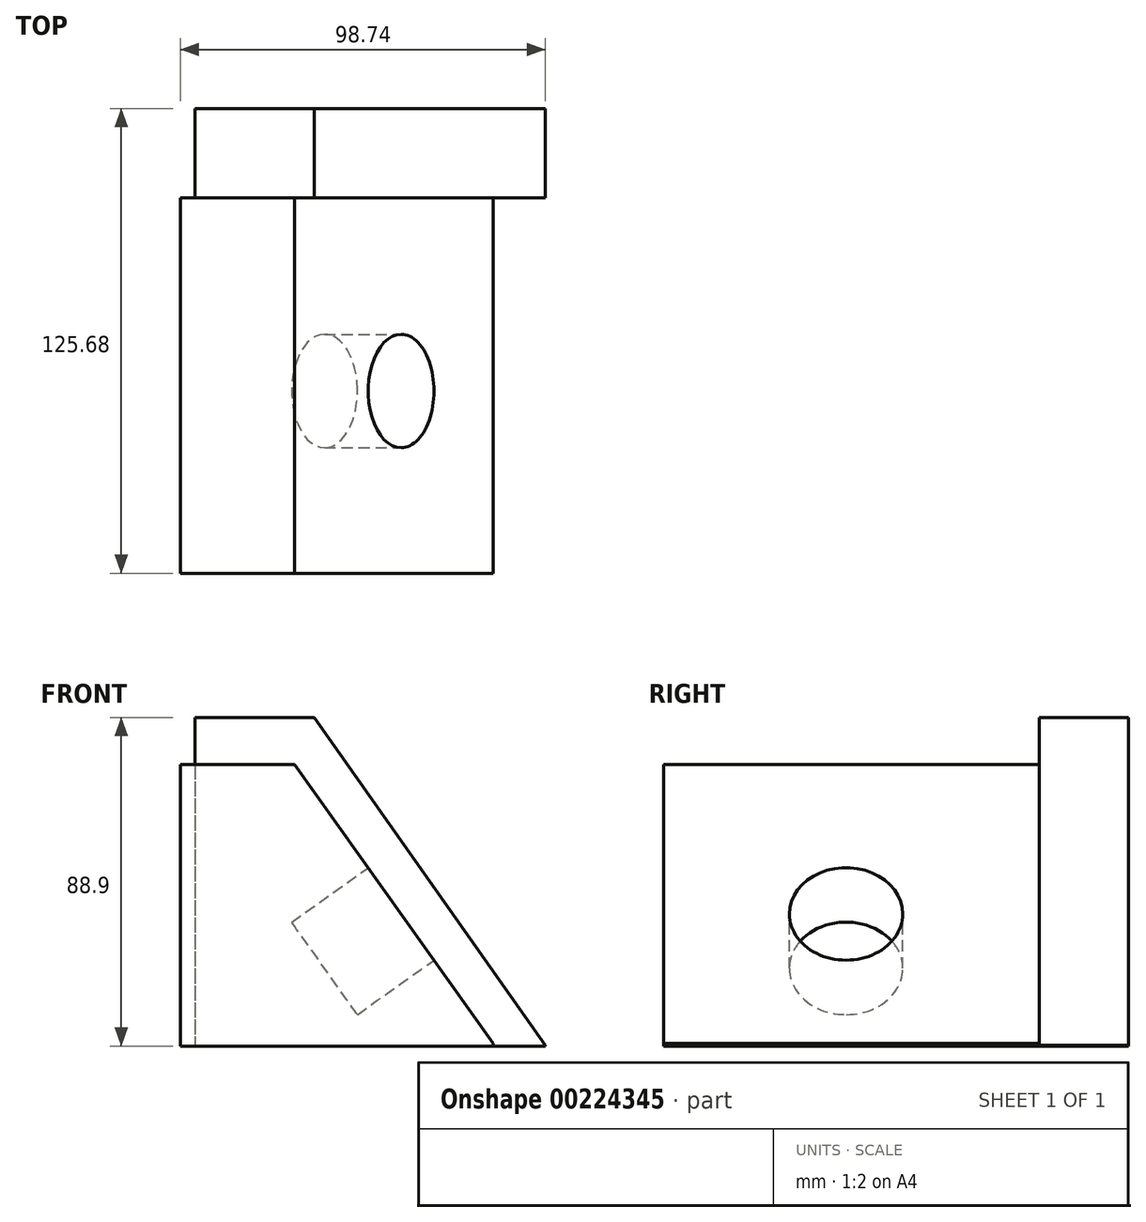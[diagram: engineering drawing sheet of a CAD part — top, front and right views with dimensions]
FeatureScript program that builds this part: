
annotation { "Feature Type Name" : "Feature", "Feature Type Description" : "" }
export const myFeature = defineFeature(function(context is Context, id is Id, definition is map)
    precondition{}
    {
        {
            var Q0;
            Q0=qCreatedBy(makeId("Top.planeOp"),FACE);
            var sketch = newSketch(context, id + "F0", { "sketchPlane" : qUnion([Q0])});
            skLineSegment(sketch, "E0.bottom", {"start": v(0, 0) * mm, "end": v(-94.83, 0) * mm});
            skLineSegment(sketch, "E0.top", {"start": v(0, 24.08) * mm, "end": v(-94.83, 24.08) * mm});
            skLineSegment(sketch, "E0.left", {"start": v(0, 0) * mm, "end": v(0, 24.08) * mm});
            skLineSegment(sketch, "E0.right", {"start": v(-94.83, 0) * mm, "end": v(-94.83, 24.08) * mm});
            skSolve(sketch);
        }
        {
            var Q0;
            Q0 = qSketchRegion(id + "F0", true);
            extrude(context, id + "F1", {"entities" : qUnion([Q0]), "depth" : 88.9 * mm});
        }
        {
            var Q0;
            Q0=makeQuery(id+"F1.opExtrude","SWEPT_FACE",FACE,{"disambiguationData":[OSD([sQuery(id+"F0.wireOp",EDGE,"E0.bottom")])]});
            var sketch = newSketch(context, id + "F2", { "sketchPlane" : qUnion([Q0])});
            skLineSegment(sketch, "E1", {"start": v(-64.9, 92.18) * mm, "end": v(19.12, -26.86) * mm});
            skLineSegment(sketch, "E2", {"start": v(19.12, -26.86) * mm, "end": v(10.84, 92.82) * mm});
            skLineSegment(sketch, "E3", {"start": v(-64.9, 92.18) * mm, "end": v(10.84, 92.82) * mm});
            skSolve(sketch);
        }
        {
            var Q0;
            {var subQ0=sQuery(id+"F2.wireOp",EDGE,"E1");var subQ1=sQuery(id+"F0.wireOp",EDGE,"E0.bottom");var subQ2=makeQuery(id+"F1.opExtrude","CAP_EDGE",EDGE,{"disambiguationData":[OSD([subQ1])],"isStart":false});var subQ3=makeQuery(id+"F2.imprint","INTERSECT",VERTEX,{"derivedFrom":[subQ2,subQ0]});Q0=makeQuery(id+"F2.imprint","IMPRINT",FACE,{"disambiguationData":[TD([[makeQuery(id+"F2.imprint","IMPRINT",EDGE,{"disambiguationData":[TD([[subQ3,-1.0]])],"derivedFrom":subQ0}),1.0]])]});}
            extrude(context, id + "F3", {"entities" : qUnion([Q0]), "operationType" : NewBodyOperationType.REMOVE, "oppositeDirection" : true, "depth" : 49.02 * mm});
        }
        {
            var Q0;
            Q0=qCreatedBy(makeId("Top.planeOp"),FACE);
            var sketch = newSketch(context, id + "F4", { "sketchPlane" : qUnion([Q0])});
            skLineSegment(sketch, "E4.bottom", {"start": v(-98.74, 0) * mm, "end": v(-14.15, 0) * mm});
            skLineSegment(sketch, "E4.top", {"start": v(-98.74, -101.6) * mm, "end": v(-14.15, -101.6) * mm});
            skLineSegment(sketch, "E4.left", {"start": v(-98.74, 0) * mm, "end": v(-98.74, -101.6) * mm});
            skLineSegment(sketch, "E4.right", {"start": v(-14.15, 0) * mm, "end": v(-14.15, -101.6) * mm});
            skSolve(sketch);
        }
        {
            var Q0;
            Q0 = qSketchRegion(id + "F4", true);
            extrude(context, id + "F5", {"entities" : qUnion([Q0]), "operationType" : NewBodyOperationType.ADD, "depth" : 76.2 * mm});
        }
        {
            var Q0;
            Q0=makeQuery(id+"F5.opExtrude","SWEPT_FACE",FACE,{"disambiguationData":[OSD([sQuery(id+"F4.wireOp",EDGE,"E4.top")])]});
            var sketch = newSketch(context, id + "F6", { "sketchPlane" : qUnion([Q0])});
            skLineSegment(sketch, "E5", {"start": v(-70.47, 79.87) * mm, "end": v(-7.66, -8.4) * mm});
            skLineSegment(sketch, "E6", {"start": v(-7.66, -8.4) * mm, "end": v(-10.63, 81.57) * mm});
            skLineSegment(sketch, "E7", {"start": v(-70.47, 79.87) * mm, "end": v(-10.63, 81.57) * mm});
            skSolve(sketch);
        }
        {
            var Q0;
            {var subQ0=sQuery(id+"F6.wireOp",EDGE,"E5");var subQ1=sQuery(id+"F4.wireOp",EDGE,"E4.top");var subQ2=makeQuery(id+"F5.opExtrude","CAP_EDGE",EDGE,{"disambiguationData":[OSD([subQ1])],"isStart":false});var subQ3=makeQuery(id+"F6.imprint","INTERSECT",VERTEX,{"derivedFrom":[subQ2,subQ0]});Q0=makeQuery(id+"F6.imprint","IMPRINT",FACE,{"disambiguationData":[TD([[makeQuery(id+"F6.imprint","IMPRINT",EDGE,{"disambiguationData":[TD([[subQ3,-1.0]])],"derivedFrom":subQ0}),1.0]])]});}
            extrude(context, id + "F7", {"entities" : qUnion([Q0]), "operationType" : NewBodyOperationType.REMOVE, "oppositeDirection" : true, "depth" : 101.6 * mm});
        }
        {
            var Q0;
            Q0=makeQuery(id+"F7.boolean.opBoolean","COPY",FACE,{"derivedFrom":makeQuery(id+"F7.opExtrude","SWEPT_FACE",FACE,{"disambiguationData":[OSD([sQuery(id+"F6.wireOp",EDGE,"E5")])]})});
            var sketch = newSketch(context, id + "F8", { "sketchPlane" : qUnion([Q0])});
            skCircle(sketch, "E8", {"center": v(-52.3, 51.76) * mm, "radius": 15.35 * mm});
            skSolve(sketch);
        }
        {
            var Q0;
            Q0 = qSketchRegion(id + "F8", true);
            extrude(context, id + "F9", {"entities" : qUnion([Q0]), "operationType" : NewBodyOperationType.REMOVE, "oppositeDirection" : true, "depth" : 25.4 * mm});
        }
    });
